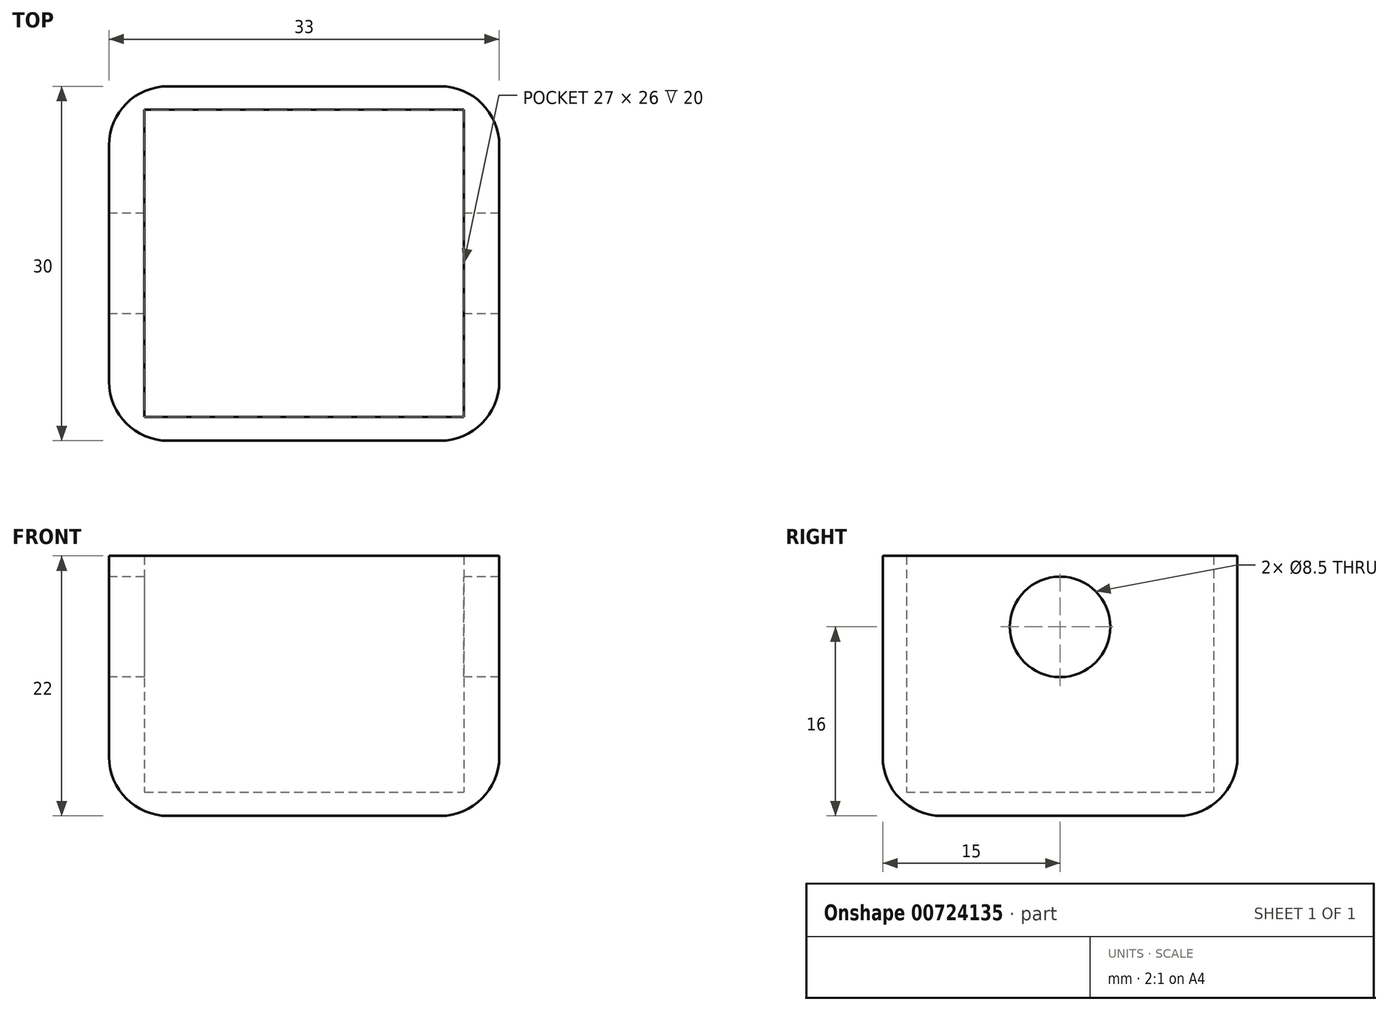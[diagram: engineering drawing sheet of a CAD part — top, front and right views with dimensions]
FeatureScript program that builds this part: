
annotation { "Feature Type Name" : "Feature", "Feature Type Description" : "" }
export const myFeature = defineFeature(function(context is Context, id is Id, definition is map)
    precondition{}
    {
        {
            var Q0;
            Q0=qCreatedBy(makeId("Top.planeOp"),FACE);
            var sketch = newSketch(context, id + "F0", { "sketchPlane" : qUnion([Q0])});
            skLineSegment(sketch, "E0.bottom", {"start": v(0, 30) * mm, "end": v(33, 30) * mm});
            skLineSegment(sketch, "E0.top", {"start": v(0, 0) * mm, "end": v(33, 0) * mm});
            skLineSegment(sketch, "E0.left", {"start": v(0, 30) * mm, "end": v(0, 0) * mm});
            skLineSegment(sketch, "E0.right", {"start": v(33, 30) * mm, "end": v(33, 0) * mm});
            skLineSegment(sketch, "E1", {"start": v(0, 15) * mm, "end": v(33, 15) * mm});
            skLineSegment(sketch, "E2", {"start": v(3, 15) * mm, "end": v(3, 30) * mm});
            skLineSegment(sketch, "E3", {"start": v(3, 28) * mm, "end": v(33, 28) * mm});
            skLineSegment(sketch, "E4", {"start": v(30, 28) * mm, "end": v(30, 0) * mm});
            skLineSegment(sketch, "E5.MirrorCS", {"start": v(3, 2) * mm, "end": v(33, 2) * mm});
            skLineSegment(sketch, "E6.MirrorCS", {"start": v(3, 15) * mm, "end": v(3, 0) * mm});
            skLineSegment(sketch, "E7", {"start": v(16.5, 15) * mm, "end": v(16.5, 26) * mm});
            skLineSegment(sketch, "E8", {"start": v(19.5, 26) * mm, "end": v(26.5, 26) * mm});
            skLineSegment(sketch, "E9", {"start": v(19.5, 15) * mm, "end": v(19.5, 26) * mm});
            skLineSegment(sketch, "E10", {"start": v(26.5, 15) * mm, "end": v(26.5, 26) * mm});
            skLineSegment(sketch, "E11.MirrorCS", {"start": v(19.5, 4) * mm, "end": v(26.5, 4) * mm});
            skLineSegment(sketch, "E12.MirrorCS", {"start": v(19.5, 15) * mm, "end": v(19.5, 4) * mm});
            skLineSegment(sketch, "E13.MirrorCS", {"start": v(26.5, 15) * mm, "end": v(26.5, 4) * mm});
            skLineSegment(sketch, "E14.MirrorCS", {"start": v(13.5, 15) * mm, "end": v(13.5, 4) * mm});
            skLineSegment(sketch, "E15.MirrorCS", {"start": v(13.5, 4) * mm, "end": v(6.5, 4) * mm});
            skLineSegment(sketch, "E16.MirrorCS", {"start": v(6.5, 15) * mm, "end": v(6.5, 4) * mm});
            skLineSegment(sketch, "E17.MirrorCS", {"start": v(6.5, 15) * mm, "end": v(6.5, 26) * mm});
            skLineSegment(sketch, "E18.MirrorCS", {"start": v(13.5, 26) * mm, "end": v(6.5, 26) * mm});
            skLineSegment(sketch, "E19.MirrorCS", {"start": v(13.5, 15) * mm, "end": v(13.5, 26) * mm});
            skLineSegment(sketch, "E20", {"start": v(3, 19) * mm, "end": v(0, 19) * mm});
            skLineSegment(sketch, "E21.MirrorCS", {"start": v(3, 11) * mm, "end": v(0, 11) * mm});
            skSolve(sketch);
        }
        {
            var Q0;
            {var subQ4=sQuery(id+"F0.wireOp",EDGE,"E20");Q0=makeQuery(id+"F0.imprint","IMPRINT",FACE,{"disambiguationData":[TD([[makeQuery(id+"F0.imprint","IMPRINT",EDGE,{"derivedFrom":subQ4}),-1.0]])]});}
            var Q1;
            {var subQ1=sQuery(id+"F0.wireOp",EDGE,"E0.bottom");var subQ5=sQuery(id+"F0.wireOp",EDGE,"E0.right");var subQ6=makeQuery(id+"F0.imprint","INTERSECT",VERTEX,{"derivedFrom":[subQ1,subQ5]});Q1=makeQuery(id+"F0.imprint","IMPRINT",FACE,{"disambiguationData":[TD([[makeQuery(id+"F0.imprint","IMPRINT",EDGE,{"disambiguationData":[TD([[subQ6,1.0]])],"derivedFrom":subQ1}),-1.0]])]});}
            var Q2;
            {var subQ0=sQuery(id+"F0.wireOp",EDGE,"E1");var subQ1=sQuery(id+"F0.wireOp",EDGE,"E0.right");var subQ2=makeQuery(id+"F0.imprint","INTERSECT",VERTEX,{"derivedFrom":[subQ1,subQ0]});Q2=makeQuery(id+"F0.imprint","IMPRINT",FACE,{"disambiguationData":[TD([[makeQuery(id+"F0.imprint","IMPRINT",EDGE,{"disambiguationData":[TD([[subQ2,1.0]])],"derivedFrom":subQ1}),-1.0]])]});}
            var Q3;
            {var subQ0=sQuery(id+"F0.wireOp",EDGE,"E1");var subQ1=sQuery(id+"F0.wireOp",EDGE,"E0.right");var subQ2=makeQuery(id+"F0.imprint","INTERSECT",VERTEX,{"derivedFrom":[subQ1,subQ0]});Q3=makeQuery(id+"F0.imprint","IMPRINT",FACE,{"disambiguationData":[TD([[makeQuery(id+"F0.imprint","IMPRINT",EDGE,{"disambiguationData":[TD([[subQ2,-1.0]])],"derivedFrom":subQ1}),-1.0]])]});}
            var Q4;
            {var subQ0=sQuery(id+"F0.wireOp",EDGE,"E0.right");var subQ1=sQuery(id+"F0.wireOp",EDGE,"E0.top");var subQ2=makeQuery(id+"F0.imprint","INTERSECT",VERTEX,{"derivedFrom":[subQ1,subQ0]});Q4=makeQuery(id+"F0.imprint","IMPRINT",FACE,{"disambiguationData":[TD([[makeQuery(id+"F0.imprint","IMPRINT",EDGE,{"disambiguationData":[TD([[subQ2,1.0]])],"derivedFrom":subQ1}),1.0]])]});}
            var Q5;
            {var subQ0=sQuery(id+"F0.wireOp",EDGE,"E4");var subQ1=sQuery(id+"F0.wireOp",EDGE,"E0.top");var subQ2=makeQuery(id+"F0.imprint","INTERSECT",VERTEX,{"derivedFrom":[subQ1,subQ0]});Q5=makeQuery(id+"F0.imprint","IMPRINT",FACE,{"disambiguationData":[TD([[makeQuery(id+"F0.imprint","IMPRINT",EDGE,{"disambiguationData":[TD([[subQ2,1.0]])],"derivedFrom":subQ1}),1.0]])]});}
            var Q6;
            {var subQ6=sQuery(id+"F0.wireOp",EDGE,"E21.MirrorCS");Q6=makeQuery(id+"F0.imprint","IMPRINT",FACE,{"disambiguationData":[TD([[makeQuery(id+"F0.imprint","IMPRINT",EDGE,{"derivedFrom":subQ6}),1.0]])]});}
            var Q7;
            {var subQ3=sQuery(id+"F0.wireOp",EDGE,"E21.MirrorCS");Q7=makeQuery(id+"F0.imprint","IMPRINT",FACE,{"disambiguationData":[TD([[makeQuery(id+"F0.imprint","IMPRINT",EDGE,{"derivedFrom":subQ3}),-1.0]])]});}
            var Q8;
            {var subQ3=sQuery(id+"F0.wireOp",EDGE,"E20");Q8=makeQuery(id+"F0.imprint","IMPRINT",FACE,{"disambiguationData":[TD([[makeQuery(id+"F0.imprint","IMPRINT",EDGE,{"derivedFrom":subQ3}),1.0]])]});}
            extrude(context, id + "F1", {"entities" : qUnion([Q0, Q1, Q2, Q3, Q4, Q5, Q6, Q7, Q8]), "depth" : 22 * mm, "offsetDistance" : 25 * mm});
        }
        {
            var Q0;
            Q0=makeQuery(id+"F0.imprint","IMPRINT",FACE,{"disambiguationData":[TD([[makeQuery(id+"F0.imprint","IMPRINT",EDGE,{"derivedFrom":sQuery(id+"F0.wireOp",EDGE,"E8")}),1.0]])]});
            var Q1;
            Q1=makeQuery(id+"F0.imprint","IMPRINT",FACE,{"disambiguationData":[TD([[makeQuery(id+"F0.imprint","IMPRINT",EDGE,{"derivedFrom":sQuery(id+"F0.wireOp",EDGE,"E11.MirrorCS")}),-1.0]])]});
            var Q2;
            {var subQ0=sQuery(id+"F0.wireOp",EDGE,"E14.MirrorCS");Q2=makeQuery(id+"F0.imprint","IMPRINT",FACE,{"disambiguationData":[TD([[makeQuery(id+"F0.imprint","IMPRINT",EDGE,{"derivedFrom":subQ0}),-1.0]])]});}
            var Q3;
            {var subQ2=sQuery(id+"F0.wireOp",EDGE,"E17.MirrorCS");Q3=makeQuery(id+"F0.imprint","IMPRINT",FACE,{"disambiguationData":[TD([[makeQuery(id+"F0.imprint","IMPRINT",EDGE,{"derivedFrom":subQ2}),-1.0]])]});}
            var Q4;
            Q4=makeQuery(id+"F0.imprint","IMPRINT",FACE,{"disambiguationData":[TD([[makeQuery(id+"F0.imprint","IMPRINT",EDGE,{"derivedFrom":sQuery(id+"F0.wireOp",EDGE,"E8")}),-1.0]])]});
            var Q5;
            Q5=makeQuery(id+"F0.imprint","IMPRINT",FACE,{"disambiguationData":[TD([[makeQuery(id+"F0.imprint","IMPRINT",EDGE,{"derivedFrom":sQuery(id+"F0.wireOp",EDGE,"E11.MirrorCS")}),1.0]])]});
            extrude(context, id + "F2", {"entities" : qUnion([Q0, Q1, Q2, Q3, Q4, Q5]), "operationType" : NewBodyOperationType.ADD, "depth" : 2 * mm, "offsetDistance" : 25 * mm});
        }
        {
            var Q0;
            Q0=qCreatedBy(makeId("Right.planeOp"),FACE);
            var sketch = newSketch(context, id + "F3", { "sketchPlane" : qUnion([Q0])});
            skLineSegment(sketch, "E22", {"start": v(0, 0) * mm, "end": v(0, 11) * mm});
            skCircle(sketch, "E23", {"center": v(15, 16) * mm, "radius": 4.25 * mm});
            skSolve(sketch);
        }
        {
            var Q0;
            Q0=makeQuery(id+"F3.imprint","IMPRINT",FACE,{"disambiguationData":[TD([[makeQuery(id+"F3.imprint","IMPRINT",EDGE,{"derivedFrom":sQuery(id+"F3.wireOp",EDGE,"E23")}),1.0]])]});
            extrude(context, id + "F4", {"entities" : qUnion([Q0]), "operationType" : NewBodyOperationType.REMOVE, "depth" : 40 * mm, "offsetDistance" : 25 * mm});
        }
        {
            var Q0;
            Q0=makeQuery(id+"F1.opExtrude","CAP_EDGE",EDGE,{"disambiguationData":[OSD([sQuery(id+"F0.wireOp",EDGE,"E0.bottom")])],"isStart":true});
            var Q1;
            Q1=makeQuery(id+"F1.opExtrude","CAP_EDGE",EDGE,{"disambiguationData":[OSD([sQuery(id+"F0.wireOp",EDGE,"E0.left")])],"isStart":true});
            var Q2;
            Q2=makeQuery(id+"F1.opExtrude","CAP_EDGE",EDGE,{"disambiguationData":[OSD([sQuery(id+"F0.wireOp",EDGE,"E0.top")])],"isStart":true});
            var Q3;
            Q3=makeQuery(id+"F1.opExtrude","CAP_EDGE",EDGE,{"disambiguationData":[OSD([sQuery(id+"F0.wireOp",EDGE,"E0.right")])],"isStart":true});
            var Q4;
            Q4=makeQuery(id+"F1.opExtrude","SWEPT_EDGE",EDGE,{"disambiguationData":[OSD([sQuery(id+"F0.wireOp",EDGE,"E0.bottom"),sQuery(id+"F0.wireOp",EDGE,"E0.right")])]});
            var Q5;
            Q5=makeQuery(id+"F1.opExtrude","SWEPT_EDGE",EDGE,{"disambiguationData":[OSD([sQuery(id+"F0.wireOp",EDGE,"E0.bottom"),sQuery(id+"F0.wireOp",EDGE,"E0.left")])]});
            var Q6;
            Q6=makeQuery(id+"F1.opExtrude","SWEPT_EDGE",EDGE,{"disambiguationData":[OSD([sQuery(id+"F0.wireOp",EDGE,"E0.top"),sQuery(id+"F0.wireOp",EDGE,"E0.left")])]});
            var Q7;
            Q7=makeQuery(id+"F1.opExtrude","SWEPT_EDGE",EDGE,{"disambiguationData":[OSD([sQuery(id+"F0.wireOp",EDGE,"E0.top"),sQuery(id+"F0.wireOp",EDGE,"E0.right")])]});
            fillet(context, id + "F5", {"entities" : qUnion([Q0, Q1, Q2, Q3, Q4, Q5, Q6, Q7]), "radius" : 5 * mm, "tangentPropagation" : true, "allowEdgeOverflow" : false});
        }
    });
